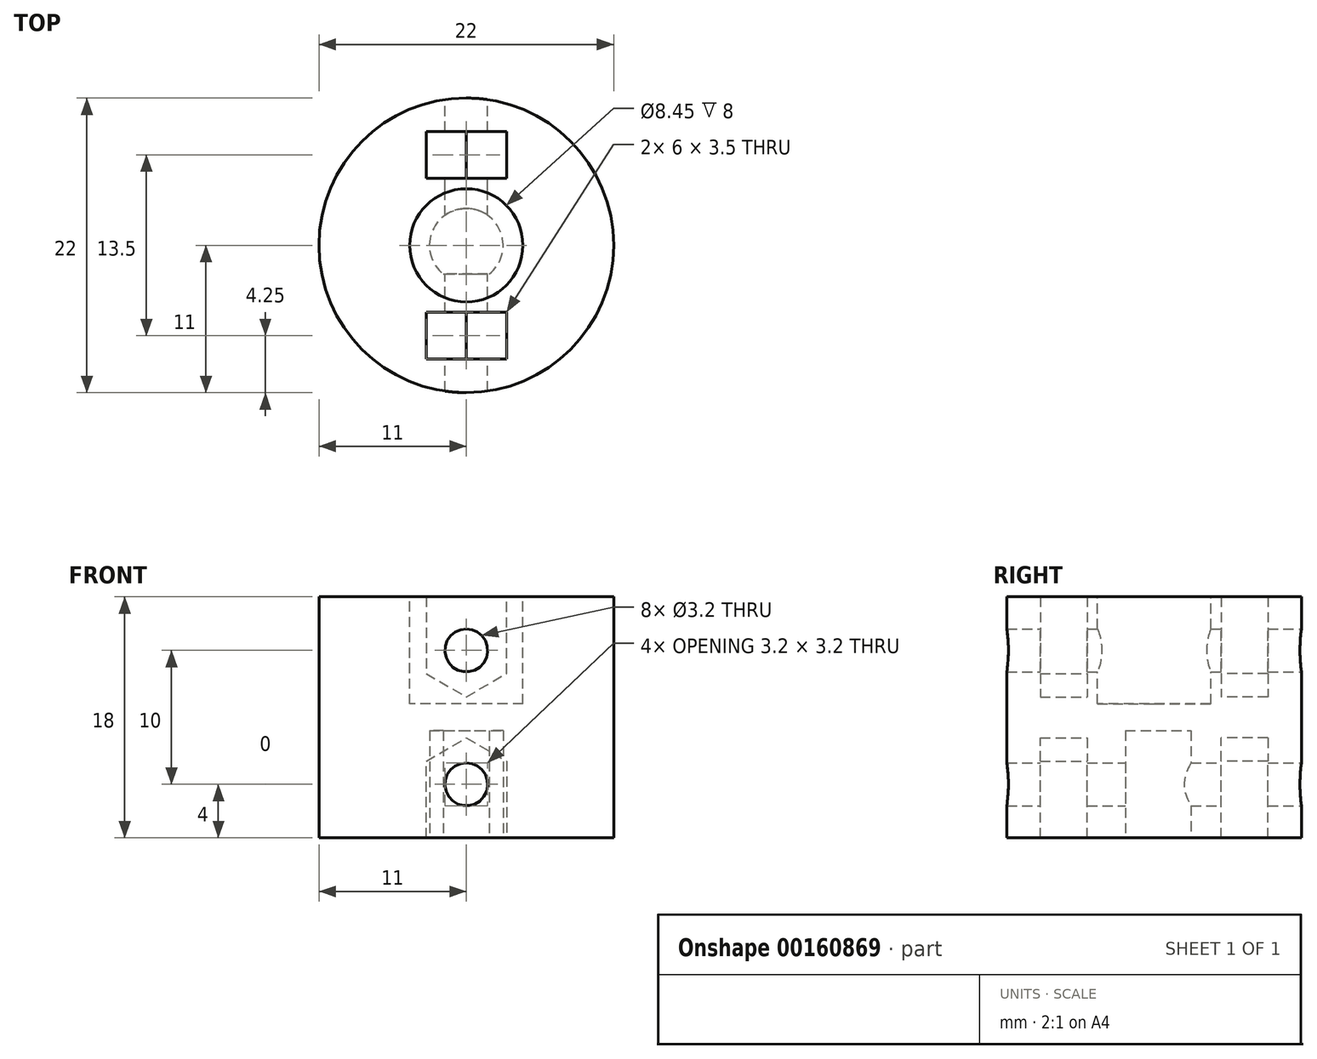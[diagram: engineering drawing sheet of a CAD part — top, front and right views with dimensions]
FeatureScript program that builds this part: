
annotation { "Feature Type Name" : "Feature", "Feature Type Description" : "" }
export const myFeature = defineFeature(function(context is Context, id is Id, definition is map)
    precondition{}
    {
        {
            var Q0;
            Q0=qCreatedBy(makeId("Top.planeOp"),FACE);
            var sketch = newSketch(context, id + "F0", { "sketchPlane" : qUnion([Q0])});
            skCircle(sketch, "E0", {"center": v(0, 0) * mm, "radius": 11 * mm});
            skSolve(sketch);
        }
        {
            var Q0;
            Q0 = qSketchRegion(id + "F0", true);
            extrude(context, id + "F1", {"entities" : qUnion([Q0]), "depth" : 18 * mm});
        }
        {
            var Q0;
            Q0=makeQuery(id+"F1.opExtrude","CAP_FACE",FACE,{"disambiguationData":[OSD([sQuery(id+"F0.wireOp",EDGE,"E0")])],"isStart":true});
            var sketch = newSketch(context, id + "F2", { "sketchPlane" : qUnion([Q0])});
            skArc(sketch, "E1", {"start": v(-1.71, 2.15) * mm, "mid": v(0, -2.75) * mm, "end": v(1.71, 2.15) * mm});
            skLineSegment(sketch, "E2", {"start": v(-1.71, 2.15) * mm, "end": v(1.71, 2.15) * mm});
            skPoint(sketch, "E3", {"position": v(0, -2.75) * mm});
            skSolve(sketch);
        }
        {
            var Q0;
            Q0 = qSketchRegion(id + "F2", true);
            extrude(context, id + "F3", {"entities" : qUnion([Q0]), "operationType" : NewBodyOperationType.REMOVE, "oppositeDirection" : true, "depth" : 8 * mm});
        }
        {
            var Q0;
            Q0=makeQuery(id+"F1.opExtrude","CAP_FACE",FACE,{"disambiguationData":[OSD([sQuery(id+"F0.wireOp",EDGE,"E0")])],"isStart":false});
            var sketch = newSketch(context, id + "F4", { "sketchPlane" : qUnion([Q0])});
            skCircle(sketch, "E4", {"center": v(0, 0) * mm, "radius": 4.22 * mm});
            skSolve(sketch);
        }
        {
            var Q0;
            Q0 = qSketchRegion(id + "F4", true);
            var Q1;
            Q1 = qSketchRegion(id + "F0", true);
            extrude(context, id + "F5", {"entities" : qUnion([Q0, Q1]), "operationType" : NewBodyOperationType.REMOVE, "oppositeDirection" : true, "depth" : 8 * mm});
        }
        {
            var Q0;
            Q0=qCreatedBy(makeId("Front.planeOp"),FACE);
            var sketch = newSketch(context, id + "F6", { "sketchPlane" : qUnion([Q0])});
            skCircle(sketch, "E5", {"center": v(0, 4) * mm, "radius": 1.6 * mm});
            skCircle(sketch, "E6", {"center": v(0, 14) * mm, "radius": 1.6 * mm});
            skPoint(sketch, "E7", {"position": v(0, 8) * mm});
            skSolve(sketch);
        }
        {
            var Q0;
            Q0 = qSketchRegion(id + "F6", true);
            extrude(context, id + "F7", {"entities" : qUnion([Q0]), "operationType" : NewBodyOperationType.REMOVE, "depth" : 25 * mm, "hasSecondDirection" : true, "secondDirectionOppositeDirection" : true, "secondDirectionDepth" : 25 * mm});
        }
        {
            var Q0;
            Q0=qCreatedBy(makeId("Front.planeOp"),FACE);
            var sketch = newSketch(context, id + "F8", { "sketchPlane" : qUnion([Q0])});
            skCircle(sketch, "E8.cCircle", {"center": v(0, 4) * mm, "radius": 3 * mm, "construction": true});
            skLineSegment(sketch, "E8.2", {"start": v(-3, 2.27) * mm, "end": v(-3, 5.73) * mm});
            skLineSegment(sketch, "E8.3", {"start": v(-3, 5.73) * mm, "end": v(0, 7.46) * mm});
            skLineSegment(sketch, "E8.4", {"start": v(0, 7.46) * mm, "end": v(3, 5.73) * mm});
            skLineSegment(sketch, "E8.5", {"start": v(3, 5.73) * mm, "end": v(3, 2.27) * mm});
            skPoint(sketch, "E8.0.midPoint", {"position": v(3, 4) * mm});
            skLineSegment(sketch, "E9", {"start": v(3, 2.27) * mm, "end": v(3, -7.73) * mm});
            skLineSegment(sketch, "E10", {"start": v(3, -7.73) * mm, "end": v(-3, -7.73) * mm});
            skLineSegment(sketch, "E11", {"start": v(-3, -7.73) * mm, "end": v(-3, 2.27) * mm});
            skLineSegment(sketch, "E12", {"start": v(-2.76, 9) * mm, "end": v(3.81, 9) * mm, "construction": true});
            skLineSegment(sketch, "E13.MirrorCS", {"start": v(-3, 12.27) * mm, "end": v(0, 10.54) * mm});
            skLineSegment(sketch, "E14.MirrorCS", {"start": v(0, 10.54) * mm, "end": v(3, 12.27) * mm});
            skLineSegment(sketch, "E15.MirrorCS", {"start": v(3, 12.27) * mm, "end": v(3, 15.73) * mm});
            skLineSegment(sketch, "E16.MirrorCS", {"start": v(3, 15.73) * mm, "end": v(3, 25.73) * mm});
            skLineSegment(sketch, "E17.MirrorCS", {"start": v(-3, 25.73) * mm, "end": v(-3, 15.73) * mm});
            skLineSegment(sketch, "E18.MirrorCS", {"start": v(-3, 15.73) * mm, "end": v(-3, 12.27) * mm});
            skLineSegment(sketch, "E19.MirrorCS", {"start": v(3, 25.73) * mm, "end": v(-3, 25.73) * mm});
            skCircle(sketch, "E20", {"center": v(0, 14) * mm, "radius": 3.46 * mm, "construction": true});
            skSolve(sketch);
        }
        {
            var Q0;
            Q0 = qSketchRegion(id + "F8", true);
            extrude(context, id + "F9", {"entities" : qUnion([Q0]), "operationType" : NewBodyOperationType.REMOVE, "depth" : 8.5 * mm, "hasSecondDirection" : true, "secondDirectionOppositeDirection" : false, "secondDirectionDepth" : 5 * mm});
        }
        {
            var Q0;
            Q0 = qSketchRegion(id + "F8", true);
            extrude(context, id + "F10", {"entities" : qUnion([Q0]), "operationType" : NewBodyOperationType.REMOVE, "oppositeDirection" : true, "depth" : 8.5 * mm, "hasSecondDirection" : true, "secondDirectionOppositeDirection" : true, "secondDirectionDepth" : 5 * mm});
        }
    });
